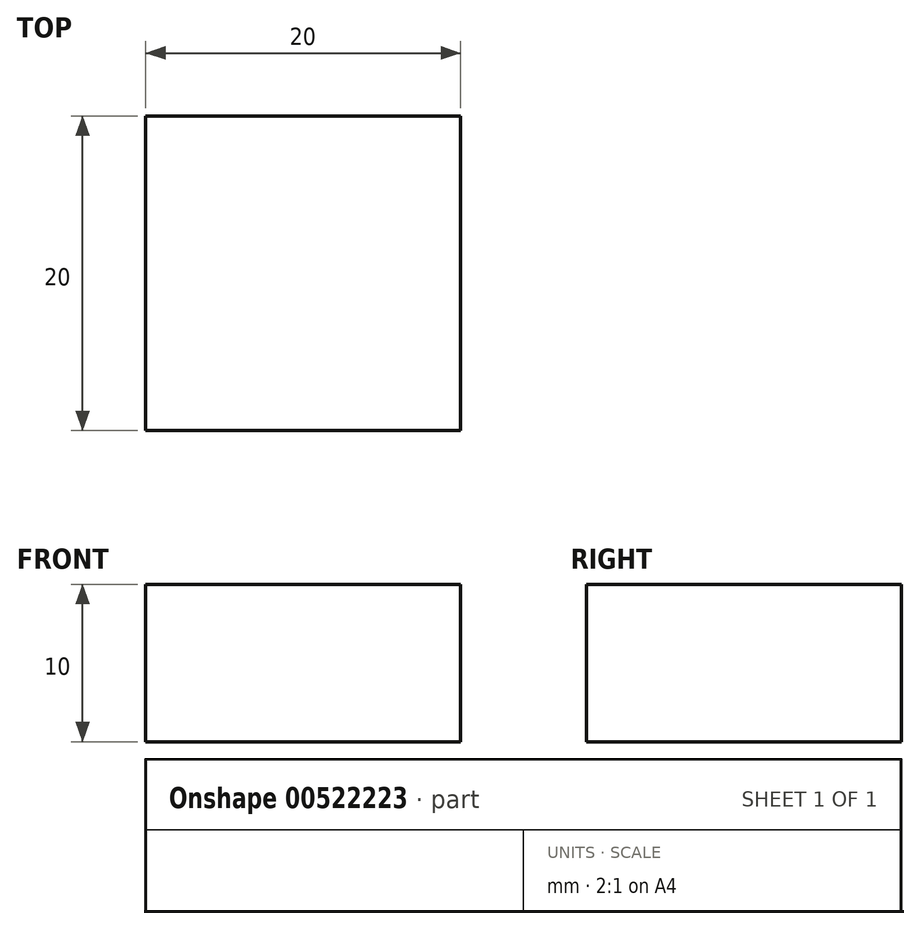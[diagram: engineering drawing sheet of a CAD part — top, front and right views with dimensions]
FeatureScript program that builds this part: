
annotation { "Feature Type Name" : "Feature", "Feature Type Description" : "" }
export const myFeature = defineFeature(function(context is Context, id is Id, definition is map)
    precondition{}
    {
        {
            var Q0;
            Q0=qCreatedBy(makeId("Top.planeOp"),FACE);
            var sketch = newSketch(context, id + "F0", { "sketchPlane" : qUnion([Q0])});
            skLineSegment(sketch, "E0.bottom", {"start": v(0, 0) * mm, "end": v(20, 0) * mm});
            skLineSegment(sketch, "E0.top", {"start": v(0, -20) * mm, "end": v(20, -20) * mm});
            skLineSegment(sketch, "E0.left", {"start": v(0, 0) * mm, "end": v(0, -20) * mm});
            skLineSegment(sketch, "E0.right", {"start": v(20, 0) * mm, "end": v(20, -20) * mm});
            skSolve(sketch);
        }
        {
            var Q0;
            Q0=makeQuery(id+"F0.imprint","IMPRINT",FACE,{"disambiguationData":[TD([[makeQuery(id+"F0.imprint","IMPRINT",EDGE,{"derivedFrom":sQuery(id+"F0.wireOp",EDGE,"E0.bottom")}),-1.0]])]});
            extrude(context, id + "F1", {"entities" : qUnion([Q0]), "depth" : 10 * mm, "offsetDistance" : 25 * mm});
        }
    });
